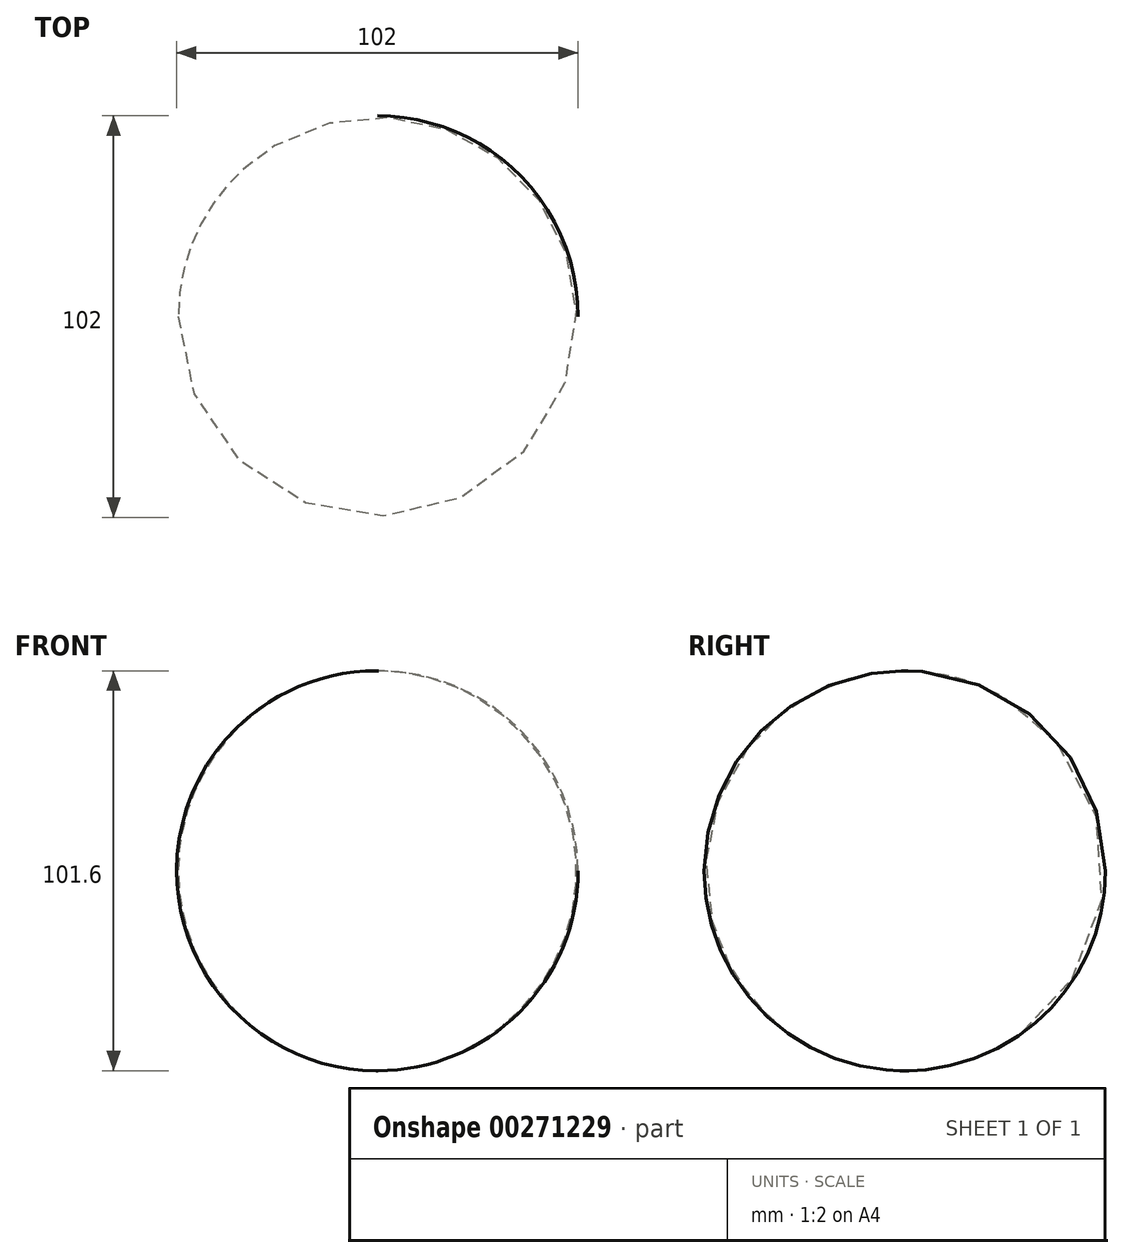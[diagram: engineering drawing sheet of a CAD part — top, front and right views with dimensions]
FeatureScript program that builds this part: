
annotation { "Feature Type Name" : "Feature", "Feature Type Description" : "" }
export const myFeature = defineFeature(function(context is Context, id is Id, definition is map)
    precondition{}
    {
        {
            var Q0;
            Q0=qCreatedBy(makeId("Front.planeOp"),FACE);
            var sketch = newSketch(context, id + "F0", { "sketchPlane" : qUnion([Q0])});
            skLineSegment(sketch, "E0", {"start": v(-0.1, 50.8) * mm, "end": v(-0.1, 50.8) * mm});
            skLineSegment(sketch, "E1", {"start": v(-0.3, -50.8) * mm, "end": v(-0.3, -50.8) * mm});
            skArc(sketch, "E2", {"start": v(-0.1, 50.8) * mm, "mid": v(-50.8, 0.1) * mm, "end": v(-0.3, -50.8) * mm});
            skLineSegment(sketch, "E3", {"start": v(-0.1, 50.8) * mm, "end": v(-0.3, -50.8) * mm});
            skSolve(sketch);
        }
        {
            var Q0;
            Q0=makeQuery(id+"F0.imprint","IMPRINT",FACE,{"disambiguationData":[TD([[makeQuery(id+"F0.imprint","IMPRINT",EDGE,{"derivedFrom":sQuery(id+"F0.wireOp",EDGE,"E2")}),1.0]])]});
            var Q1;
            Q1=sQuery(id+"F0.wireOp",EDGE,"E3");
            revolve(context, id + "F1", {"entities" : qUnion([Q0]), "axis" : qUnion([Q1]), "revolveType" : RevolveType.FULL});
        }
    });
